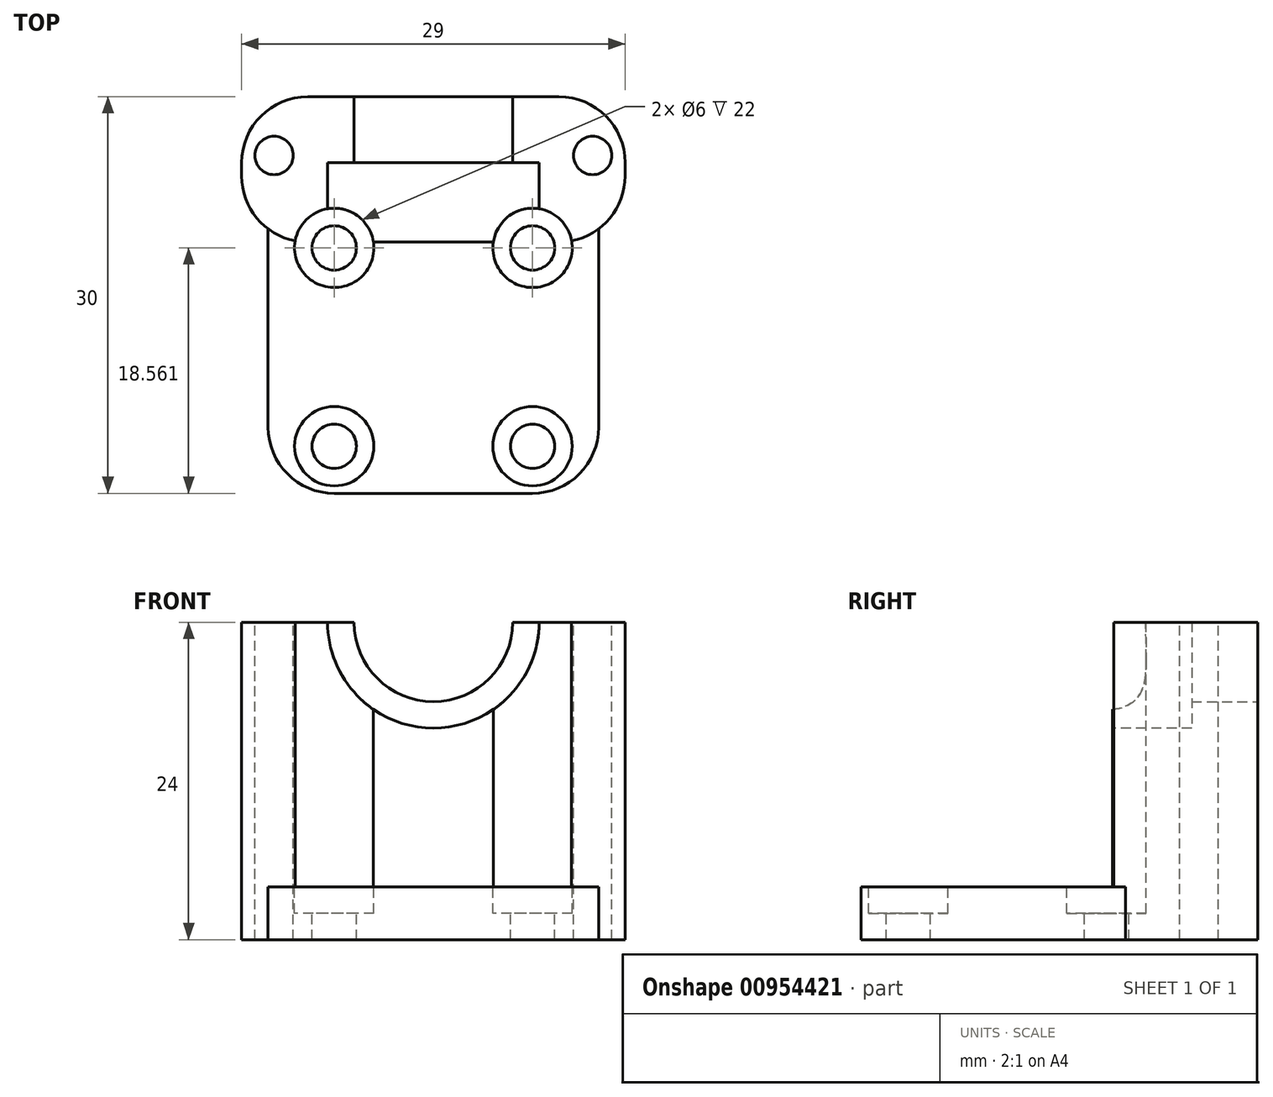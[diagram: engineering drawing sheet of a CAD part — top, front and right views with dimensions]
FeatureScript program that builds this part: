
annotation { "Feature Type Name" : "Feature", "Feature Type Description" : "" }
export const myFeature = defineFeature(function(context is Context, id is Id, definition is map)
    precondition{}
    {
        {
            var Q0;
            Q0=qCreatedBy(makeId("Top.planeOp"),FACE);
            var sketch = newSketch(context, id + "F0", { "sketchPlane" : qUnion([Q0])});
            skLineSegment(sketch, "E0.bottom", {"start": v(0, 0) * mm, "end": v(25, 0) * mm});
            skLineSegment(sketch, "E0.top", {"start": v(0, 30) * mm, "end": v(25, 30) * mm});
            skLineSegment(sketch, "E0.left", {"start": v(0, 0) * mm, "end": v(0, 30) * mm});
            skLineSegment(sketch, "E0.right", {"start": v(25, 0) * mm, "end": v(25, 30) * mm});
            skSolve(sketch);
        }
        {
            var Q0;
            Q0=qSketchRegion(id+"F0",true);
            extrude(context, id + "F1", {"entities" : qUnion([Q0]), "depth" : 4 * mm});
        }
        {
            var Q0;
            Q0=makeQuery(id+"F1.opExtrude","CAP_FACE",FACE,{"disambiguationData":[OSD([sQuery(id+"F0.wireOp",EDGE,"E0.bottom"),sQuery(id+"F0.wireOp",EDGE,"E0.top"),sQuery(id+"F0.wireOp",EDGE,"E0.left"),sQuery(id+"F0.wireOp",EDGE,"E0.right")])],"isStart":false});
            var sketch = newSketch(context, id + "F2", { "sketchPlane" : qUnion([Q0])});
            skCircle(sketch, "E1", {"center": v(5, 18.56) * mm, "radius": 1.68 * mm});
            skCircle(sketch, "E2", {"center": v(20, 18.56) * mm, "radius": 1.68 * mm});
            skCircle(sketch, "E3", {"center": v(5, 3.56) * mm, "radius": 1.68 * mm});
            skCircle(sketch, "E4", {"center": v(20, 3.56) * mm, "radius": 1.68 * mm});
            skLineSegment(sketch, "E5", {"start": v(5, 18.56) * mm, "end": v(0, 18.56) * mm});
            skLineSegment(sketch, "E6", {"start": v(20, 3.56) * mm, "end": v(25, 3.56) * mm});
            skCircle(sketch, "E7", {"center": v(5, 18.56) * mm, "radius": 3 * mm});
            skCircle(sketch, "E8", {"center": v(20, 18.56) * mm, "radius": 3 * mm});
            skCircle(sketch, "E9", {"center": v(5, 3.56) * mm, "radius": 3 * mm});
            skCircle(sketch, "E10", {"center": v(20, 3.56) * mm, "radius": 3 * mm});
            skSolve(sketch);
        }
        {
            var Q0;
            Q0=makeQuery(id+"F2.imprint","IMPRINT",FACE,{"disambiguationData":[TD([[makeQuery(id+"F2.imprint","IMPRINT",EDGE,{"derivedFrom":sQuery(id+"F2.wireOp",EDGE,"E1")}),1.0]])]});
            var Q1;
            Q1=makeQuery(id+"F2.imprint","IMPRINT",FACE,{"disambiguationData":[TD([[makeQuery(id+"F2.imprint","IMPRINT",EDGE,{"derivedFrom":sQuery(id+"F2.wireOp",EDGE,"E2")}),1.0]])]});
            var Q2;
            Q2=makeQuery(id+"F2.imprint","IMPRINT",FACE,{"disambiguationData":[TD([[makeQuery(id+"F2.imprint","IMPRINT",EDGE,{"derivedFrom":sQuery(id+"F2.wireOp",EDGE,"E4")}),1.0]])]});
            var Q3;
            Q3=makeQuery(id+"F2.imprint","IMPRINT",FACE,{"disambiguationData":[TD([[makeQuery(id+"F2.imprint","IMPRINT",EDGE,{"derivedFrom":sQuery(id+"F2.wireOp",EDGE,"E3")}),1.0]])]});
            extrude(context, id + "F3", {"entities" : qUnion([Q0, Q1, Q2, Q3]), "operationType" : NewBodyOperationType.REMOVE, "oppositeDirection" : true, "depth" : 25 * mm});
        }
        {
            var Q0;
            Q0=makeQuery(id+"F1.opExtrude","CAP_FACE",FACE,{"disambiguationData":[OSD([sQuery(id+"F0.wireOp",EDGE,"E0.bottom"),sQuery(id+"F0.wireOp",EDGE,"E0.top"),sQuery(id+"F0.wireOp",EDGE,"E0.left"),sQuery(id+"F0.wireOp",EDGE,"E0.right")])],"isStart":false});
            var sketch = newSketch(context, id + "F4", { "sketchPlane" : qUnion([Q0])});
            skLineSegment(sketch, "E11.bottom", {"start": v(0, 30) * mm, "end": v(25, 30) * mm});
            skLineSegment(sketch, "E11.top", {"start": v(0, 19) * mm, "end": v(25, 19) * mm});
            skLineSegment(sketch, "E11.left", {"start": v(0, 30) * mm, "end": v(0, 19) * mm});
            skLineSegment(sketch, "E11.right", {"start": v(25, 30) * mm, "end": v(25, 19) * mm});
            skSolve(sketch);
        }
        {
            var Q0;
            Q0=qSketchRegion(id+"F4",true);
            extrude(context, id + "F5", {"entities" : qUnion([Q0]), "operationType" : NewBodyOperationType.ADD, "depth" : 20 * mm, "offsetDistance" : 25 * mm});
        }
        {
            var Q0;
            Q0=makeQuery(id+"F5.boolean.opBoolean","MERGE",FACE,{"derivedFrom":[makeQuery(id+"F1.opExtrude","SWEPT_FACE",FACE,{"disambiguationData":[OSD([sQuery(id+"F0.wireOp",EDGE,"E0.top")])]}),makeQuery(id+"F5.opExtrude","SWEPT_FACE",FACE,{"disambiguationData":[OSD([sQuery(id+"F4.wireOp",EDGE,"E11.bottom")])]})]});
            var sketch = newSketch(context, id + "F6", { "sketchPlane" : qUnion([Q0])});
            skCircle(sketch, "E12", {"center": v(-12.5, 24) * mm, "radius": 6 * mm});
            skSolve(sketch);
        }
        {
            var Q0;
            {var subQ0=makeQuery(id+"F5.opExtrude","CAP_EDGE",EDGE,{"disambiguationData":[OSD([sQuery(id+"F4.wireOp",EDGE,"E11.bottom")])],"isStart":false});var subQ1=sQuery(id+"F6.wireOp",EDGE,"E12");var subQ3=makeQuery(id+"F6.imprint","INTERSECT",VERTEX,{"disambiguationData":[OD(0.0)],"derivedFrom":[subQ0,subQ1]});Q0=makeQuery(id+"F6.imprint","IMPRINT",FACE,{"disambiguationData":[TD([[makeQuery(id+"F6.imprint","IMPRINT",EDGE,{"disambiguationData":[TD([[subQ3,1.0]])],"derivedFrom":subQ1}),1.0]])]});}
            extrude(context, id + "F7", {"entities" : qUnion([Q0]), "operationType" : NewBodyOperationType.REMOVE, "oppositeDirection" : true, "depth" : 6 * mm});
        }
        {
            var Q0;
            Q0=makeQuery(id+"F5.opExtrude","SWEPT_FACE",FACE,{"disambiguationData":[OSD([sQuery(id+"F4.wireOp",EDGE,"E11.top")])]});
            var sketch = newSketch(context, id + "F8", { "sketchPlane" : qUnion([Q0])});
            skCircle(sketch, "E13", {"center": v(12.5, 24) * mm, "radius": 8 * mm});
            skSolve(sketch);
        }
        {
            var Q0;
            Q0=qSketchRegion(id+"F8",true);
            extrude(context, id + "F9", {"entities" : qUnion([Q0]), "operationType" : NewBodyOperationType.REMOVE, "oppositeDirection" : true, "depth" : 6 * mm});
        }
        {
            var Q0;
            Q0=makeQuery(id+"F2.imprint","IMPRINT",FACE,{"disambiguationData":[TD([[makeQuery(id+"F2.imprint","IMPRINT",EDGE,{"derivedFrom":sQuery(id+"F2.wireOp",EDGE,"E1")}),-1.0]])]});
            var Q1;
            Q1=makeQuery(id+"F2.imprint","IMPRINT",FACE,{"disambiguationData":[TD([[makeQuery(id+"F2.imprint","IMPRINT",EDGE,{"derivedFrom":sQuery(id+"F2.wireOp",EDGE,"E2")}),-1.0]])]});
            var Q2;
            Q2=makeQuery(id+"F2.imprint","IMPRINT",FACE,{"disambiguationData":[TD([[makeQuery(id+"F2.imprint","IMPRINT",EDGE,{"derivedFrom":sQuery(id+"F2.wireOp",EDGE,"E4")}),-1.0]])]});
            var Q3;
            Q3=makeQuery(id+"F2.imprint","IMPRINT",FACE,{"disambiguationData":[TD([[makeQuery(id+"F2.imprint","IMPRINT",EDGE,{"derivedFrom":sQuery(id+"F2.wireOp",EDGE,"E3")}),-1.0]])]});
            extrude(context, id + "F10", {"entities" : qUnion([Q0, Q1, Q2, Q3]), "operationType" : NewBodyOperationType.REMOVE, "oppositeDirection" : true, "depth" : 2 * mm});
        }
        {
            var Q0;
            Q0=makeQuery(id+"F5.boolean.opBoolean","MERGE",FACE,{"derivedFrom":[makeQuery(id+"F1.opExtrude","SWEPT_FACE",FACE,{"disambiguationData":[OSD([sQuery(id+"F0.wireOp",EDGE,"E0.left")])]}),makeQuery(id+"F5.opExtrude","SWEPT_FACE",FACE,{"disambiguationData":[OSD([sQuery(id+"F4.wireOp",EDGE,"E11.left")])]})]});
            var sketch = newSketch(context, id + "F11", { "sketchPlane" : qUnion([Q0])});
            skLineSegment(sketch, "E14.bottom", {"start": v(-30, 0) * mm, "end": v(-19, 0) * mm});
            skLineSegment(sketch, "E14.top", {"start": v(-30, 24) * mm, "end": v(-19, 24) * mm});
            skLineSegment(sketch, "E14.left", {"start": v(-30, 0) * mm, "end": v(-30, 24) * mm});
            skLineSegment(sketch, "E14.right", {"start": v(-19, 0) * mm, "end": v(-19, 24) * mm});
            skSolve(sketch);
        }
        {
            var Q0;
            Q0=qSketchRegion(id+"F11",true);
            extrude(context, id + "F12", {"entities" : qUnion([Q0]), "operationType" : NewBodyOperationType.ADD, "depth" : 2 * mm});
        }
        {
            var Q0;
            Q0=makeQuery(id+"F1.opExtrude","SWEPT_EDGE",EDGE,{"disambiguationData":[OSD([sQuery(id+"F0.wireOp",EDGE,"E0.bottom"),sQuery(id+"F0.wireOp",EDGE,"E0.left")])]});
            var Q1;
            Q1=makeQuery(id+"F1.opExtrude","SWEPT_EDGE",EDGE,{"disambiguationData":[OSD([sQuery(id+"F0.wireOp",EDGE,"E0.bottom"),sQuery(id+"F0.wireOp",EDGE,"E0.right")])]});
            fillet(context, id + "F13", {"entities" : qUnion([Q0, Q1]), "radius" : 5 * mm, "tangentPropagation" : true, "allowEdgeOverflow" : false});
        }
        {
            var Q0;
            Q0=makeQuery(id+"F5.boolean.opBoolean","MERGE",FACE,{"derivedFrom":[makeQuery(id+"F1.opExtrude","SWEPT_FACE",FACE,{"disambiguationData":[OSD([sQuery(id+"F0.wireOp",EDGE,"E0.right")])]}),makeQuery(id+"F5.opExtrude","SWEPT_FACE",FACE,{"disambiguationData":[OSD([sQuery(id+"F4.wireOp",EDGE,"E11.right")])]})]});
            var sketch = newSketch(context, id + "F14", { "sketchPlane" : qUnion([Q0])});
            skLineSegment(sketch, "E15.bottom", {"start": v(30, 0) * mm, "end": v(19, 0) * mm});
            skLineSegment(sketch, "E15.top", {"start": v(30, 24) * mm, "end": v(19, 24) * mm});
            skLineSegment(sketch, "E15.left", {"start": v(30, 0) * mm, "end": v(30, 24) * mm});
            skLineSegment(sketch, "E15.right", {"start": v(19, 0) * mm, "end": v(19, 24) * mm});
            skSolve(sketch);
        }
        {
            var Q0;
            Q0=qSketchRegion(id+"F14",true);
            extrude(context, id + "F15", {"entities" : qUnion([Q0]), "operationType" : NewBodyOperationType.ADD, "depth" : 2 * mm});
        }
        {
            var Q0;
            Q0=qSketchRegion(id+"F14",true);
            extrude(context, id + "F16", {"entities" : qUnion([Q0]), "operationType" : NewBodyOperationType.ADD, "depth" : 2 * mm});
        }
        {
            var Q0;
            {var subQ0=sQuery(id+"F4.wireOp",EDGE,"E11.bottom");var subQ1=sQuery(id+"F4.wireOp",EDGE,"E11.top");var subQ2=sQuery(id+"F4.wireOp",EDGE,"E11.left");Q0=makeQuery(id+"F9.boolean.opBoolean","SPLIT",FACE,{"disambiguationData":[TD([makeQuery(id+"F1.opExtrude","SWEPT_FACE",FACE,{"disambiguationData":[OSD([sQuery(id+"F0.wireOp",EDGE,"E0.left")])]})])],"derivedFrom":makeQuery(id+"F5.opExtrude","CAP_FACE",FACE,{"disambiguationData":[OSD([subQ0,subQ1,subQ2,sQuery(id+"F4.wireOp",EDGE,"E11.right")])],"isStart":false})});}
            var sketch = newSketch(context, id + "F17", { "sketchPlane" : qUnion([Q0])});
            skCircle(sketch, "E16", {"center": v(0.45, 25.55) * mm, "radius": 1.45 * mm});
            skCircle(sketch, "E17", {"center": v(24.55, 25.55) * mm, "radius": 1.45 * mm});
            skSolve(sketch);
        }
        {
            var Q0;
            Q0=qSketchRegion(id+"F17",true);
            extrude(context, id + "F18", {"entities" : qUnion([Q0]), "operationType" : NewBodyOperationType.REMOVE, "oppositeDirection" : true, "depth" : 25 * mm});
        }
        {
            var Q0;
            Q0=makeQuery(id+"F12.opExtrude","CAP_EDGE",EDGE,{"disambiguationData":[OSD([sQuery(id+"F11.wireOp",EDGE,"E14.left")])],"isStart":false});
            var Q1;
            Q1=makeQuery(id+"F12.opExtrude","CAP_EDGE",EDGE,{"disambiguationData":[OSD([sQuery(id+"F11.wireOp",EDGE,"E14.right")])],"isStart":false});
            var Q2;
            Q2=makeQuery(id+"F15.opExtrude","CAP_EDGE",EDGE,{"disambiguationData":[OSD([sQuery(id+"F14.wireOp",EDGE,"E15.right")])],"isStart":false});
            var Q3;
            Q3=makeQuery(id+"F15.opExtrude","CAP_EDGE",EDGE,{"disambiguationData":[OSD([sQuery(id+"F14.wireOp",EDGE,"E15.left")])],"isStart":false});
            fillet(context, id + "F19", {"entities" : qUnion([Q0, Q1, Q2, Q3]), "radius" : 5 * mm, "tangentPropagation" : true, "allowEdgeOverflow" : false});
        }
        {
            var Q0;
            Q0=makeQuery(id+"F2.imprint","IMPRINT",FACE,{"disambiguationData":[TD([[makeQuery(id+"F2.imprint","IMPRINT",EDGE,{"derivedFrom":sQuery(id+"F2.wireOp",EDGE,"E1")}),-1.0]])]});
            var Q1;
            Q1=makeQuery(id+"F2.imprint","IMPRINT",FACE,{"disambiguationData":[TD([[makeQuery(id+"F2.imprint","IMPRINT",EDGE,{"derivedFrom":sQuery(id+"F2.wireOp",EDGE,"E2")}),-1.0]])]});
            var Q2;
            Q2=makeQuery(id+"F2.imprint","IMPRINT",FACE,{"disambiguationData":[TD([[makeQuery(id+"F2.imprint","IMPRINT",EDGE,{"derivedFrom":sQuery(id+"F2.wireOp",EDGE,"E1")}),1.0]])]});
            var Q3;
            Q3=makeQuery(id+"F2.imprint","IMPRINT",FACE,{"disambiguationData":[TD([[makeQuery(id+"F2.imprint","IMPRINT",EDGE,{"derivedFrom":sQuery(id+"F2.wireOp",EDGE,"E2")}),1.0]])]});
            extrude(context, id + "F20", {"entities" : qUnion([Q0, Q1, Q2, Q3]), "operationType" : NewBodyOperationType.REMOVE, "depth" : 25 * mm});
        }
    });
